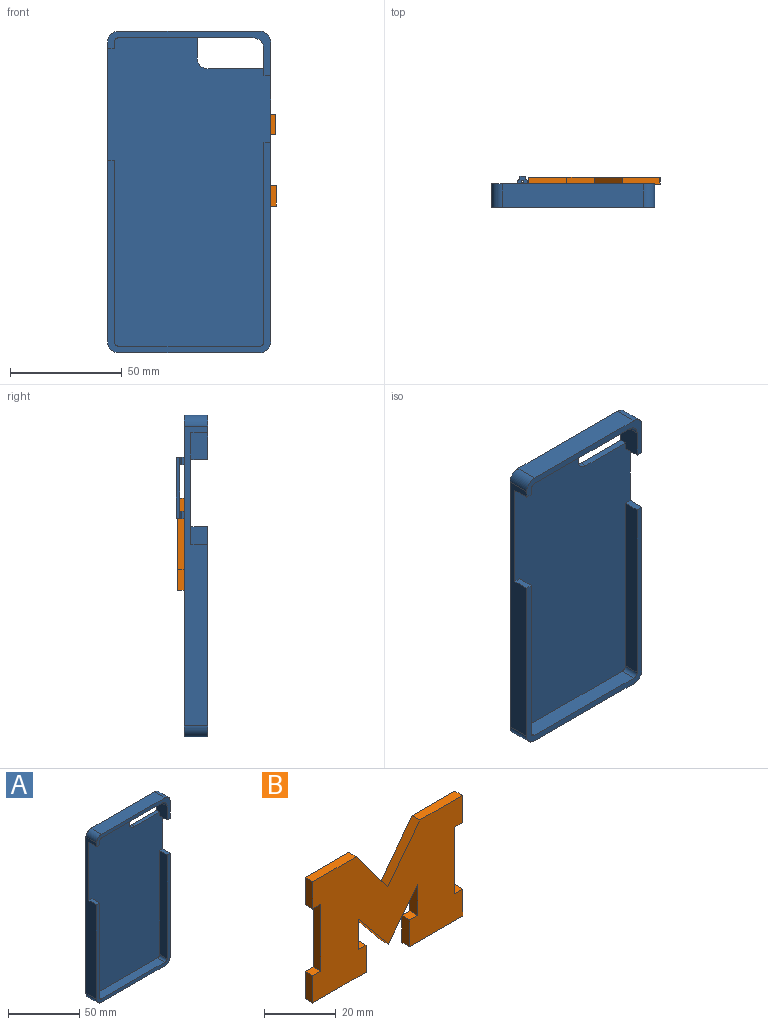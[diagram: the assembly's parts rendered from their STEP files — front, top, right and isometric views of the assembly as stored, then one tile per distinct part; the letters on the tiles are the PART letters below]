
ASSEMBLY  parts=2 mates=1
PART A: 88 faces, bbox 73.1x14x144.3 mm
  f0: plane 144.3x73.1mm, normal (0,1,0), area 4683.7mm2, adj f5,f7,f10,f11,f12,f13,f14,f15
  f1: cylinder r=1mm len=3.2mm, axis (0,0,1), area 5mm2, adj f2,f61,f62,f64,f75,f76
  f2: plane 3.2x2.5mm, normal (0,1,0), area 0.2mm2, adj f1,f62,f64,f71,f76,f77
  f3: plane 73.1x20mm, normal (0,-1,0), area 280.8mm2, adj f5,f6,f7,f10,f12,f15,f16,f19
  f4: plane 89.3x7.5mm, normal (-1,0,0), area 669.8mm2, adj f8,f9,f22,f30
  f5: plane 134.3x10.5mm, normal (1,0,0), area 1185.1mm2, adj f0,f3,f8,f9,f14,f15,f29,f30
  f6: plane 7.5x3mm, normal (1,0,0), area 22.5mm2, adj f3,f8,f20,f27
  f7: plane 134.3x10.5mm, normal (-1,0,0), area 1035.1mm2, adj f0,f3,f8,f9,f12,f13,f27,f28
  f8: plane 138.3x73.1mm, normal (0,-1,0), area 9102.7mm2, adj f4,f5,f6,f7,f16,f17,f18,f19
  f9: plane 94.3x73.1mm, normal (0,-1,0), area 734.1mm2, adj f4,f5,f7,f11,f13,f14,f17,f18
  f10: plane 63.1x10.5mm, normal (0,0,1), area 662.6mm2, adj f0,f3,f12,f15
  f11: plane 63.1x10.5mm, normal (0,0,-1), area 662.6mm2, adj f0,f9,f13,f14
  f12: cylinder r=5mm len=10.5mm, axis (0,-1,0), area 82.5mm2, adj f0,f3,f7,f10
  f13: cylinder r=5mm len=10.5mm, axis (0,1,0), area 82.5mm2, adj f0,f7,f9,f11
  f14: cylinder r=5mm len=10.5mm, axis (0,-1,0), area 82.5mm2, adj f0,f5,f9,f11
  f15: cylinder r=5mm len=10.5mm, axis (0,1,0), area 82.5mm2, adj f0,f3,f5,f10
  f16: plane 60.1x10.5mm, normal (0,0,-1), area 525.8mm2, adj f0,f3,f8,f20,f24,f26
  f17: plane 81.3x7.5mm, normal (1,0,0), area 609.7mm2, adj f8,f9,f21,f28
  f18: plane 63.1x7.5mm, normal (0,0,1), area 473.3mm2, adj f8,f9,f21,f22
  f19: plane 12x10.5mm, normal (-1,0,0), area 117mm2, adj f0,f3,f8,f23,f26,f29
  f20: cylinder r=2mm len=7.5mm, axis (0,-1,0), area 23.6mm2, adj f3,f6,f8,f16
  f21: cylinder r=2mm len=7.5mm, axis (0,1,0), area 23.6mm2, adj f8,f9,f17,f18
  f22: cylinder r=2mm len=7.5mm, axis (0,-1,0), area 23.6mm2, adj f4,f8,f9,f18
  f23: plane 25x3mm, normal (0,0,1), area 75mm2, adj f0,f8,f19,f25
  f24: plane 9x3mm, normal (1,0,0), area 27mm2, adj f0,f8,f16,f25
  f25: cylinder r=5mm len=5mm, axis (0,-1,0), area 23.6mm2, adj f0,f8,f23,f24
  f26: cylinder r=5mm len=10.5mm, axis (0,-1,0), area 82.5mm2, adj f0,f3,f16,f19
  f27: plane 7.5x3mm, normal (0,0,-1), area 22.5mm2, adj f3,f6,f7,f8
  f28: plane 7.5x3mm, normal (0,0,1), area 22.5mm2, adj f7,f8,f9,f17
  f29: plane 7.5x3mm, normal (0,0,-1), area 22.5mm2, adj f3,f5,f8,f19
  f30: plane 7.5x3mm, normal (0,0,1), area 22.5mm2, adj f4,f5,f8,f9
  f31: plane 9.25x1.5mm, normal (1,0,0), area 13.9mm2, adj f0,f32,f54,f55
  f32: plane 3.17x1.5mm, normal (0,0,-1), area 4.7mm2, adj f0,f31,f33,f55
  f33: plane 22.72x1.5mm, normal (1,0,0), area 34.1mm2, adj f0,f32,f34,f55
  f34: plane 3.2x1.5mm, normal (0,0,1), area 4.8mm2, adj f0,f33,f35,f55
  f35: plane 9.26x1.5mm, normal (1,0,0), area 13.9mm2, adj f0,f34,f36,f55
  f36: plane 17.13x1.5mm, normal (0,0,-1), area 25.7mm2, adj f0,f35,f37,f55
  f37: plane 16.46x12.4mm, normal (-0.8,0,-0.6), area 30.9mm2, adj f0,f36,f38,f55
  f38: plane 16.46x12.58mm, normal (0.79,0,-0.61), area 31.1mm2, adj f0,f37,f39,f55
  f39: plane 16.73x1.5mm, normal (0,0,-1), area 25.1mm2, adj f0,f38,f40,f55
  f40: plane 9.26x1.5mm, normal (-1,0,0), area 13.9mm2, adj f0,f39,f41,f55
  f41: plane 3.06x1.5mm, normal (0,0,1), area 4.6mm2, adj f0,f40,f42,f55
  f42: plane 22.72x1.5mm, normal (-1,0,0), area 34.1mm2, adj f0,f41,f43,f55
  f43: plane 3.27x1.5mm, normal (0,0,-1), area 4.9mm2, adj f0,f42,f44,f55
  f44: plane 9.17x1.5mm, normal (-1,0,0), area 13.8mm2, adj f0,f43,f45,f55
  f45: plane 21x1.5mm, normal (0,0,1), area 31.5mm2, adj f0,f44,f46,f55
  f46: plane 9.17x1.5mm, normal (1,0,0), area 13.8mm2, adj f0,f45,f47,f55
  f47: plane 3.18x1.5mm, normal (0,0,-1), area 4.8mm2, adj f0,f46,f48,f55
  f48: plane 10.4x1.5mm, normal (1,0,0), area 15.6mm2, adj f0,f47,f49,f55
  f49: plane 14.42x11.57mm, normal (-0.78,0,0.63), area 27.7mm2, adj f0,f48,f50,f55
  f50: plane 14.42x11.79mm, normal (0.77,0,0.63), area 27.9mm2, adj f0,f49,f51,f55
  f51: plane 10.41x1.5mm, normal (-1,0,0), area 15.6mm2, adj f0,f50,f52,f55
  f52: plane 3.1x1.5mm, normal (0,0,-1), area 4.6mm2, adj f0,f51,f53,f55
  f53: plane 9.24x1.5mm, normal (-1,0,0), area 13.9mm2, adj f0,f52,f54,f55
  f54: plane 20.95x1.5mm, normal (0,0,1), area 31.4mm2, adj f0,f31,f53,f55
  f55: plane 59.06x41.23mm, normal (0,1,0), area 1846mm2, adj f31,f32,f33,f34,f35,f36,f37,f38
  f56: plane 19x1mm, normal (-1,0,0), area 19mm2, adj f0,f57,f59,f60
  f57: plane 55x1mm, normal (0,0,1), area 55mm2, adj f0,f56,f58,f60
  f58: plane 19x1mm, normal (1,0,0), area 19mm2, adj f0,f57,f59,f60
  f59: plane 55x1mm, normal (0,0,-1), area 55mm2, adj f0,f56,f58,f60
  f60: plane 55x19mm, normal (0,1,0), area 1045mm2, adj f56,f57,f58,f59
  f61: plane 3.2x1mm, normal (1,0,0), area 3.2mm2, adj f0,f1,f62,f64
  f62: plane 4.5x2mm, normal (0,0,-1), area 7.8mm2, adj f0,f1,f2,f61,f63,f70,f71
  f63: plane 3.2x1mm, normal (-1,0,0), area 3.2mm2, adj f0,f62,f64,f71
  f64: plane 4.5x2mm, normal (0,0,1), area 7.8mm2, adj f0,f1,f2,f61,f63,f70,f71,f74
  f65: plane 4.5x3.5mm, normal (0,0,1), area 11.5mm2, adj f0,f66,f68,f69,f72,f73,f75,f77
  f66: plane 3.2x1mm, normal (1,0,0), area 3.2mm2, adj f0,f65,f67,f72
  f67: plane 4.5x2mm, normal (0,0,-1), area 7.8mm2, adj f0,f66,f68,f69,f72,f73,f74
  f68: plane 3.2x1mm, normal (-1,0,0), area 3.2mm2, adj f0,f65,f67,f73
  f69: cylinder r=0.5mm len=3.2mm, axis (0,0,1), area 10.1mm2, adj f65,f67
  f70: cylinder r=0.5mm len=3.2mm, axis (0,0,1), area 10.1mm2, adj f62,f64
  f71: cylinder r=1mm len=3.2mm, axis (0,0,-1), area 5mm2, adj f2,f62,f63,f64
  f72: cylinder r=1mm len=3.2mm, axis (0,0,1), area 5mm2, adj f65,f66,f67,f75
  f73: cylinder r=1mm len=3.2mm, axis (0,0,-1), area 5mm2, adj f65,f67,f68,f77
  f74: plane 21x2.5mm, normal (0,-1,0), area 52.5mm2, adj f64,f67,f75,f77
  f75: plane 27.32x1.5mm, normal (1,0,0), area 41mm2, adj f1,f65,f72,f74,f76,f78
  f76: plane 2.5x1.5mm, normal (0,0,-1), area 3.8mm2, adj f1,f2,f75,f77,f78
  f77: plane 27.32x1.5mm, normal (-1,0,0), area 41mm2, adj f2,f65,f73,f74,f76,f78
  f78: plane 27.32x2.5mm, normal (0,1,0), area 68.3mm2, adj f65,f75,f76,f77
  f79: plane 45x1mm, normal (0,0,-1), area 45mm2, adj f0,f83,f84,f87
  f80: plane 20x1mm, normal (-1,0,0), area 20mm2, adj f0,f83,f84,f85
  f81: plane 45x1mm, normal (0,0,1), area 45mm2, adj f0,f83,f85,f86
  f82: plane 20x1mm, normal (1,0,0), area 20mm2, adj f0,f83,f86,f87
  f83: plane 65x40mm, normal (0,1,0), area 2514.2mm2, adj f79,f80,f81,f82,f84,f85,f86,f87
  f84: cylinder r=10mm len=10mm, axis (0,1,0), area 15.7mm2, adj f0,f79,f80,f83
  f85: cylinder r=10mm len=10mm, axis (0,-1,0), area 15.7mm2, adj f0,f80,f81,f83
  f86: cylinder r=10mm len=10mm, axis (0,1,0), area 15.7mm2, adj f0,f81,f82,f83
  f87: cylinder r=10mm len=10mm, axis (0,-1,0), area 15.7mm2, adj f0,f79,f82,f83
PART B: 26 faces, bbox 59.1x3x41.2 mm
  f0: plane 9.25x3mm, normal (-1,0,0), area 27.7mm2, adj f1,f23,f24,f25
  f1: plane 20.95x3mm, normal (0,0,-1), area 62.8mm2, adj f0,f2,f24,f25
  f2: plane 9.24x3mm, normal (1,0,0), area 27.7mm2, adj f1,f3,f24,f25
  f3: plane 3.1x3mm, normal (0,0,1), area 9.3mm2, adj f2,f4,f24,f25
  f4: plane 10.41x3mm, normal (1,0,0), area 31.2mm2, adj f3,f5,f24,f25
  f5: plane 14.42x11.79mm, normal (-0.77,0,-0.63), area 55.9mm2, adj f4,f6,f24,f25
  f6: plane 14.42x11.57mm, normal (0.78,0,-0.63), area 55.5mm2, adj f5,f7,f24,f25
  f7: plane 10.4x3mm, normal (-1,0,0), area 31.2mm2, adj f6,f8,f24,f25
  f8: plane 3.18x3mm, normal (0,0,1), area 9.5mm2, adj f7,f9,f24,f25
  f9: plane 9.17x3mm, normal (-1,0,0), area 27.5mm2, adj f8,f10,f24,f25
  f10: plane 21x3mm, normal (0,0,-1), area 63mm2, adj f9,f11,f24,f25
  f11: plane 9.17x3mm, normal (1,0,0), area 27.5mm2, adj f10,f12,f24,f25
  f12: plane 3.27x3mm, normal (0,0,1), area 9.8mm2, adj f11,f13,f24,f25
  f13: plane 22.72x3mm, normal (1,0,0), area 68.2mm2, adj f12,f14,f24,f25
  f14: plane 3.06x3mm, normal (0,0,-1), area 9.2mm2, adj f13,f15,f24,f25
  f15: plane 9.26x3mm, normal (1,0,0), area 27.8mm2, adj f14,f16,f24,f25
  f16: plane 16.73x3mm, normal (0,0,1), area 50.2mm2, adj f15,f17,f24,f25
  f17: plane 16.46x12.58mm, normal (-0.79,0,0.61), area 62.1mm2, adj f16,f18,f24,f25
  f18: plane 16.46x12.4mm, normal (0.8,0,0.6), area 61.8mm2, adj f17,f19,f24,f25
  f19: plane 17.13x3mm, normal (0,0,1), area 51.4mm2, adj f18,f20,f24,f25
  f20: plane 9.26x3mm, normal (-1,0,0), area 27.8mm2, adj f19,f21,f24,f25
  f21: plane 3.2x3mm, normal (0,0,-1), area 9.6mm2, adj f20,f22,f24,f25
  f22: plane 22.72x3mm, normal (-1,0,0), area 68.2mm2, adj f21,f23,f24,f25
  f23: plane 3.17x3mm, normal (0,0,1), area 9.5mm2, adj f0,f22,f24,f25
  f24: plane 59.06x41.23mm, normal (0,-1,0), area 1846mm2, adj f0,f1,f2,f3,f4,f5,f6,f7
  f25: plane 59.06x41.23mm, normal (0,1,0), area 1846mm2, adj f0,f1,f2,f3,f4,f5,f6,f7
PLACE A t=(59.48,8.71,-31.75)mm
PLACE B t=(66.58,11.71,-18.49)mm
MATE fastened A.f0 <-> B.f24  axis (0,1,0) through (57.44,8.71,-18.49)mm
